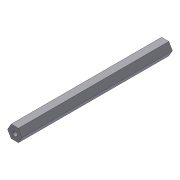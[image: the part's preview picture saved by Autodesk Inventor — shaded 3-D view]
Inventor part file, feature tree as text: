
AUTODESK INVENTOR PART (.ipt)
format: ipt  version: 2012 (Build 160160000, 160)  size: 89,600 bytes
history: native  units: in
note: dims shown in document units (in); Inventor stores cm internally (conversion verified against a paired STEP export)
features: extrude x3, sketch x3
ambient origin geometry x8: Origin, YZ Plane, XZ Plane, XY Plane, X Axis, Y Axis, Z Axis, Center Point
bodies: Solid1 (feature_tree)
feature tree (6):
  extrude  "Extrusion1"  Depth=6.0in TaperAngle=0.0deg
  extrude  "Extrusion4"  Depth=0.5in TaperAngle=0.0deg
  extrude  "Extrusion5"  Depth=0.5in TaperAngle=0.0deg
  sketch  "Sketch1"  dims[d0=0.5in d1=6.0in d2=0.0in]
  sketch  "Sketch4"  dims[d10=0.192in d11=0.5in d12=0.0in]
  sketch  "Sketch5"  dims[d13=0.192in d14=0.5in d15=0.0in]
